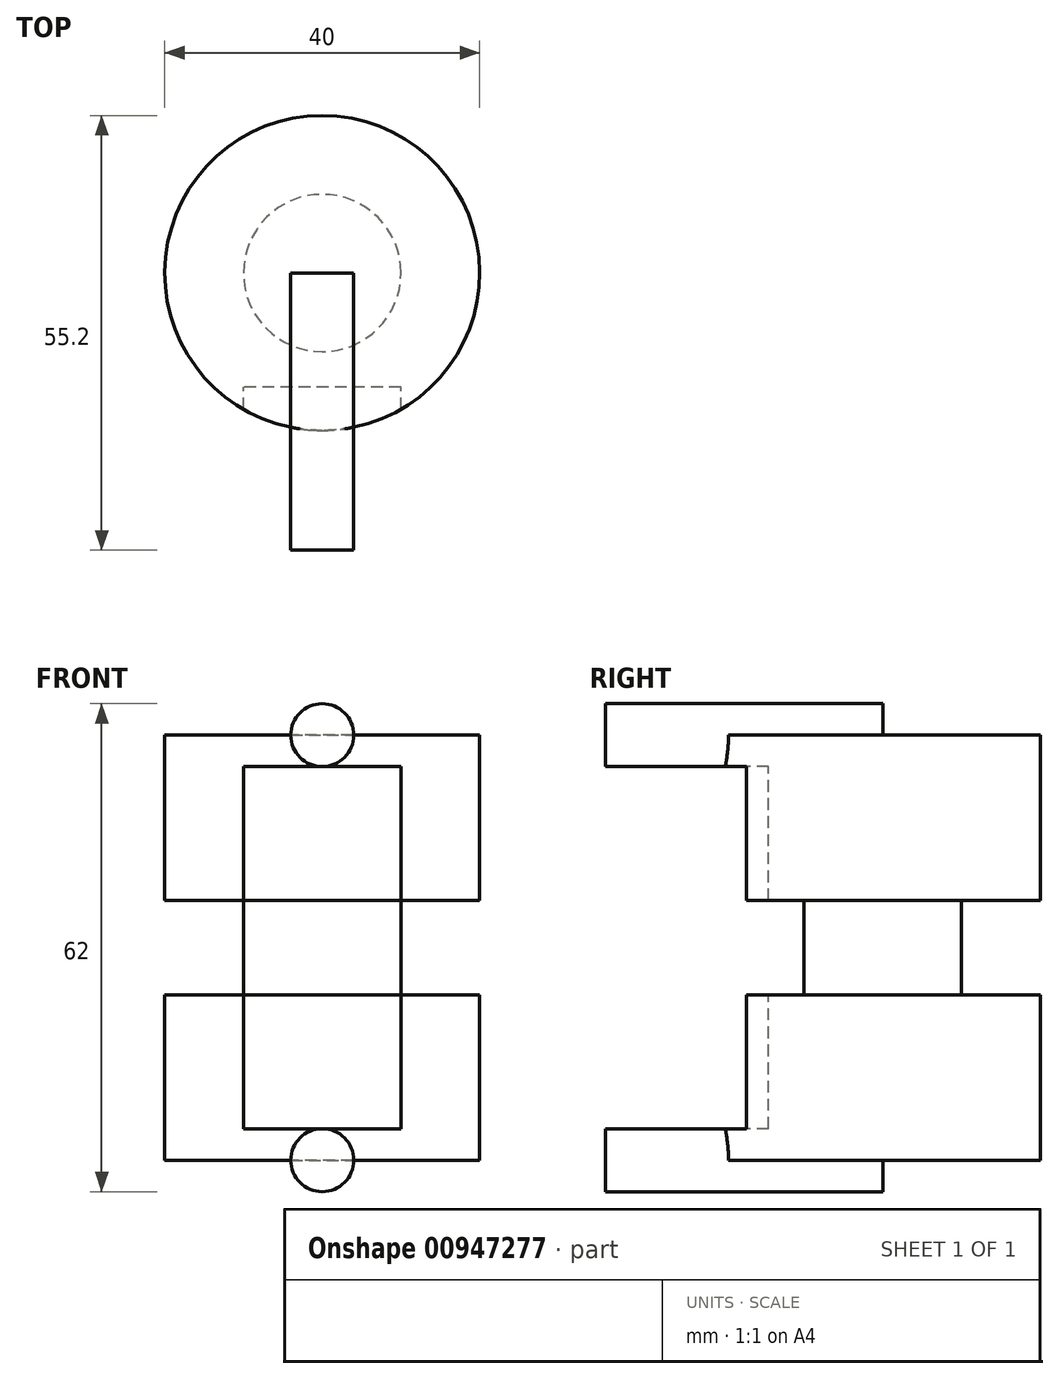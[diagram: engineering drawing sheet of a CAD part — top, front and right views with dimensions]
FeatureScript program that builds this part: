
annotation { "Feature Type Name" : "Feature", "Feature Type Description" : "" }
export const myFeature = defineFeature(function(context is Context, id is Id, definition is map)
    precondition{}
    {
        {
            var Q0;
            Q0=qCreatedBy(makeId("Top.planeOp"),FACE);
            var sketch = newSketch(context, id + "F0", { "sketchPlane" : qUnion([Q0])});
            skCircle(sketch, "E0", {"center": v(0, 0) * mm, "radius": 20 * mm});
            skSolve(sketch);
        }
        {
            var Q0;
            Q0=makeQuery(id+"F0.imprint","IMPRINT",FACE,{"disambiguationData":[TD([[makeQuery(id+"F0.imprint","IMPRINT",EDGE,{"derivedFrom":sQuery(id+"F0.wireOp",EDGE,"E0")}),1.0]])]});
            extrude(context, id + "F1", {"entities" : qUnion([Q0]), "endBound" : BoundingType.SYMMETRIC, "depth" : 54 * mm, "offsetDistance" : 25 * mm});
        }
        {
            var Q0;
            Q0=qCreatedBy(makeId("Front.planeOp"),FACE);
            var sketch = newSketch(context, id + "F2", { "sketchPlane" : qUnion([Q0])});
            skLineSegment(sketch, "E1.bottom", {"start": v(10, -6) * mm, "end": v(29.39, -6) * mm});
            skLineSegment(sketch, "E1.top", {"start": v(10, 6) * mm, "end": v(29.39, 6) * mm});
            skLineSegment(sketch, "E1.left", {"start": v(10, -6) * mm, "end": v(10, 6) * mm});
            skLineSegment(sketch, "E1.right", {"start": v(29.39, -6) * mm, "end": v(29.39, 6) * mm});
            skSolve(sketch);
        }
        {
            var Q0;
            Q0=qCreatedBy(makeId("Front.planeOp"),FACE);
            var sketch = newSketch(context, id + "F3", { "sketchPlane" : qUnion([Q0])});
            skLineSegment(sketch, "E2", {"start": v(0, 38.56) * mm, "end": v(0, -38.2) * mm, "construction": true});
            skSolve(sketch);
        }
        {
            var Q0;
            Q0=makeQuery(id+"F2.imprint","IMPRINT",FACE,{"disambiguationData":[TD([[makeQuery(id+"F2.imprint","IMPRINT",EDGE,{"derivedFrom":sQuery(id+"F2.wireOp",EDGE,"E1.bottom")}),1.0]])]});
            var Q1;
            Q1=sQuery(id+"F3.wireOp",EDGE,"E2");
            var Q2;
            Q2=sQuery(id+"F3.wireOp",EDGE,"E2");
            revolve(context, id + "F4", {"operationType" : NewBodyOperationType.REMOVE, "surfaceOperationType" : NewSurfaceOperationType.NEW, "entities" : qUnion([Q0]), "surfaceEntities" : qUnion([Q1]), "axis" : qUnion([Q2]), "revolveType" : RevolveType.FULL, "oppositeDirection" : true});
        }
        {
            var Q0;
            Q0=qCreatedBy(makeId("Front.planeOp"),FACE);
            var sketch = newSketch(context, id + "F5", { "sketchPlane" : qUnion([Q0])});
            skCircle(sketch, "E3", {"center": v(0, 27) * mm, "radius": 4 * mm});
            skCircle(sketch, "E4", {"center": v(0, -27) * mm, "radius": 4 * mm});
            skSolve(sketch);
        }
        {
            var Q0;
            Q0 = qSketchRegion(id + "F5", true);
            extrude(context, id + "F6", {"entities" : qUnion([Q0]), "operationType" : NewBodyOperationType.ADD, "depth" : 35.2 * mm, "offsetDistance" : 25 * mm});
        }
        {
            var Q0;
            Q0=makeQuery(id+"F4.boolean.opBoolean","COPY",FACE,{"derivedFrom":makeQuery(id+"F4.opRevolve","SWEPT_FACE",FACE,{"disambiguationData":[OSD([sQuery(id+"F2.wireOp",EDGE,"E1.bottom")])]})});
            var sketch = newSketch(context, id + "F7", { "sketchPlane" : qUnion([Q0])});
            skLineSegment(sketch, "E5.bottom", {"start": v(-10, -14.5) * mm, "end": v(10, -14.5) * mm});
            skLineSegment(sketch, "E5.top", {"start": v(-10, -25.96) * mm, "end": v(10, -25.96) * mm});
            skLineSegment(sketch, "E5.left", {"start": v(-10, -14.5) * mm, "end": v(-10, -25.96) * mm});
            skLineSegment(sketch, "E5.right", {"start": v(10, -14.5) * mm, "end": v(10, -25.96) * mm});
            skSolve(sketch);
        }
        {
            var Q0;
            Q0 = qSketchRegion(id + "F7", true);
            extrude(context, id + "F8", {"entities" : qUnion([Q0]), "operationType" : NewBodyOperationType.REMOVE, "oppositeDirection" : true, "depth" : 17 * mm, "offsetDistance" : 25 * mm, "hasSecondDirection" : true, "secondDirectionOppositeDirection" : false, "secondDirectionDepth" : 29 * mm});
        }
    });
